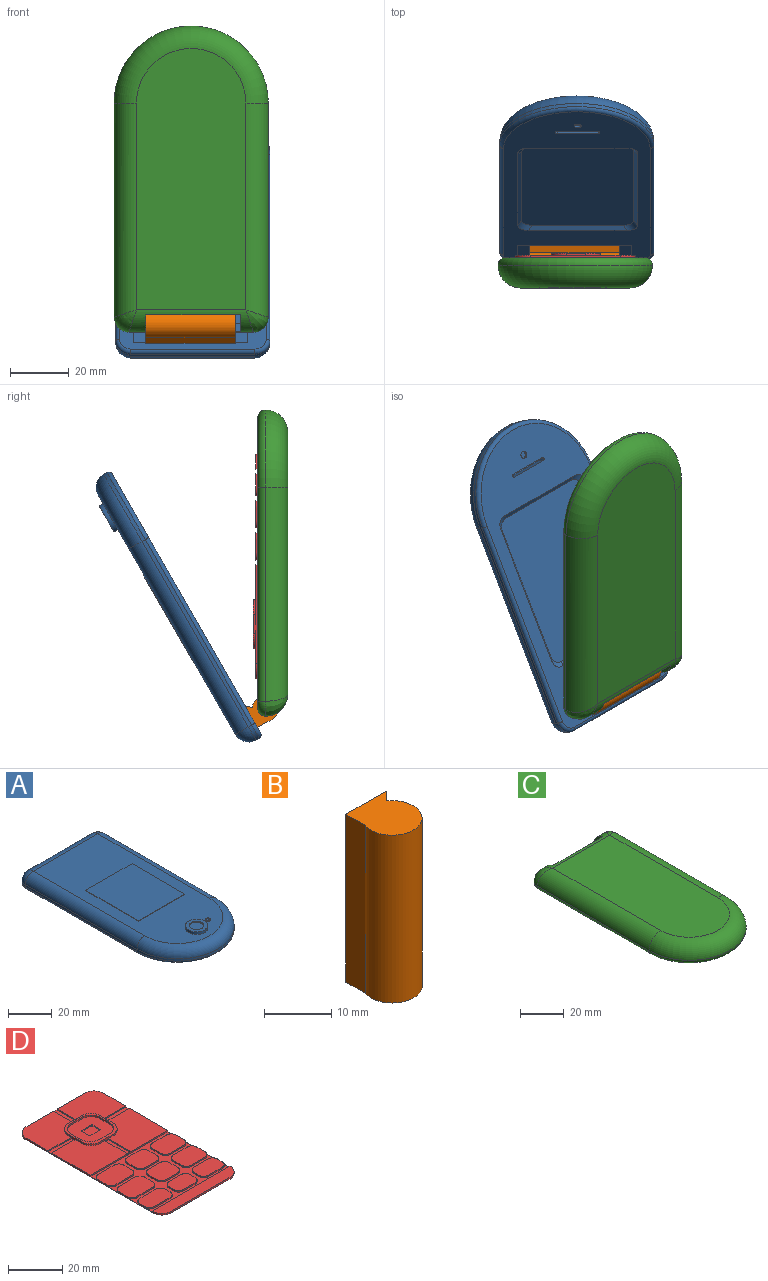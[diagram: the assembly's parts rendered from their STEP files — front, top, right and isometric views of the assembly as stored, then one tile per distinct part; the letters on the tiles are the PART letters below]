
ASSEMBLY  parts=4 mates=3
PART A: 58 faces, bbox 56.6x106.5x9.7 mm
  f0: plane 101.35x49.78mm, normal (0,0,-1), area 2202.3mm2, adj f14,f15,f16,f17,f18,f19,f21,f22
  f1: plane 42.16x1.27mm, normal (0,1,0), area 53.5mm2, adj f6,f7,f11,f17
  f2: plane 72.64x1.27mm, normal (-1,0,0), area 92.3mm2, adj f5,f6,f12,f14
  f3: plane 72.64x1.27mm, normal (1,0,0), area 92.3mm2, adj f5,f7,f8,f18
  f4: plane 93.73x42.16mm, normal (0,0,1), area 2641.5mm2, adj f8,f10,f11,f12,f43,f47,f51,f52
  f5: cylinder r=26.16mm len=52.32mm, axis (0,0,1), area 104.4mm2, adj f2,f3,f10,f16
  f6: cylinder r=5.08mm len=5.08mm, axis (0,0,1), area 10.1mm2, adj f1,f2,f13,f15
  f7: cylinder r=5.08mm len=5.08mm, axis (0,0,-1), area 10.1mm2, adj f1,f3,f9,f19
  f8: cylinder r=5.08mm len=72.64mm, axis (0,-1,0), area 579.7mm2, adj f3,f4,f9,f10
  f9: sphere r=5.08mm, area 40.5mm2, adj f7,f8,f11
  f10: torus R=21.08mm, axis (0,0,1), area 609.6mm2, adj f4,f5,f8,f12
  f11: cylinder r=5.08mm len=42.16mm, axis (1,0,0), area 336.5mm2, adj f1,f4,f9,f13
  f12: cylinder r=5.08mm len=72.64mm, axis (0,1,0), area 579.7mm2, adj f2,f4,f10,f13
  f13: sphere r=5.08mm, area 40.5mm2, adj f6,f11,f12
  f14: cylinder r=1.27mm len=72.64mm, axis (0,-1,0), area 144.9mm2, adj f0,f2,f15,f16
  f15: torus R=3.81mm, axis (0,0,1), area 14.5mm2, adj f0,f6,f14,f17
  f16: torus R=24.89mm, axis (0,0,1), area 161.1mm2, adj f0,f5,f14,f18
  f17: cylinder r=1.27mm len=42.16mm, axis (-1,0,0), area 84.1mm2, adj f0,f1,f15,f19
  f18: cylinder r=1.27mm len=72.64mm, axis (0,1,0), area 144.9mm2, adj f0,f3,f16,f19
  f19: torus R=3.81mm, axis (0,0,1), area 14.5mm2, adj f0,f7,f17,f18
  f20: plane 53.34x38.1mm, normal (0,0,-1), area 2022.6mm2, adj f21,f22,f23,f24,f25,f26,f27,f28
  f21: plane 33.46x1.27mm, normal (0,0.71,-0.71), area 57.8mm2, adj f0,f20,f25,f26
  f22: plane 48.7x1.27mm, normal (0.71,0,-0.71), area 85.2mm2, adj f0,f20,f25,f27
  f23: plane 48.7x1.27mm, normal (-0.71,0,-0.71), area 85.2mm2, adj f0,f20,f26,f28
  f24: plane 33.46x1.27mm, normal (0,-0.71,-0.71), area 57.8mm2, adj f0,f20,f27,f28
  f25: cylinder r=5.08mm len=5.42mm, axis (-0.58,-0.58,-0.58), area 11.7mm2, adj f0,f20,f21,f22
  f26: cylinder r=5.08mm len=5.42mm, axis (0.58,-0.58,-0.58), area 11.7mm2, adj f0,f20,f21,f23
  f27: cylinder r=5.08mm len=5.42mm, axis (0.58,-0.58,0.58), area 11.7mm2, adj f0,f20,f22,f24
  f28: cylinder r=5.08mm len=5.42mm, axis (-0.58,-0.58,0.58), area 11.7mm2, adj f0,f20,f23,f24
  f29: plane 38.61x0.03mm, normal (0,-1,0), area 1mm2, adj f0,f30,f32,f33
  f30: plane 7.46x0.03mm, normal (-1,0,0), area 0.2mm2, adj f0,f29,f31,f33
  f31: plane 38.61x0.03mm, normal (0,1,0), area 1mm2, adj f0,f30,f32,f33
  f32: plane 7.46x0.03mm, normal (1,0,0), area 0.2mm2, adj f0,f29,f31,f33
  f33: plane 38.61x7.46mm, normal (0,0,-1), area 287.8mm2, adj f29,f30,f31,f32
  f34: plane 13.92x2.54mm, normal (0,1,0), area 35.4mm2, adj f0,f38,f39,f42
  f35: plane 2.54x0.14mm, normal (1,0,0), area 0.4mm2, adj f0,f38,f39,f40
  f36: plane 13.92x2.54mm, normal (0,-1,0), area 35.4mm2, adj f0,f38,f40,f41
  f37: plane 2.54x0.14mm, normal (-1,0,0), area 0.4mm2, adj f0,f38,f41,f42
  f38: plane 14.94x1.16mm, normal (0,0,-1), area 17.1mm2, adj f34,f35,f36,f37,f39,f40,f41,f42
  f39: cylinder r=0.51mm len=2.54mm, axis (0,0,-1), area 2mm2, adj f0,f34,f35,f38
  f40: cylinder r=0.51mm len=2.54mm, axis (0,0,1), area 2mm2, adj f0,f35,f36,f38
  f41: cylinder r=0.51mm len=2.54mm, axis (0,0,-1), area 2mm2, adj f0,f36,f37,f38
  f42: cylinder r=0.51mm len=2.54mm, axis (0,0,1), area 2mm2, adj f0,f34,f37,f38
  f43: cylinder r=5.08mm len=10.16mm, axis (0,0,-1), area 48.6mm2, adj f4,f44
  f44: plane 10.16x10.16mm, normal (0,0,1), area 47.4mm2, adj f43,f45
  f45: cylinder r=3.27mm len=6.54mm, axis (0,0,1), area 10.4mm2, adj f44,f46
  f46: plane 6.54x6.54mm, normal (0,0,1), area 33.6mm2, adj f45
  f47: cylinder r=1.17mm len=2.35mm, axis (0,0,-1), area 2.1mm2, adj f4,f48
  f48: plane 2.35x2.35mm, normal (0,0,1), area 2.1mm2, adj f47,f49
  f49: cylinder r=0.84mm len=1.67mm, axis (0,0,1), area 1.3mm2, adj f48,f50
  f50: plane 1.67x1.67mm, normal (0,0,1), area 2.2mm2, adj f49
  f51: plane 30.08x0.25mm, normal (0,1,0), area 7.6mm2, adj f4,f52,f54,f55
  f52: plane 34.38x0.25mm, normal (-1,0,0), area 8.7mm2, adj f4,f51,f53,f55
  f53: plane 30.08x0.25mm, normal (0,-1,0), area 7.6mm2, adj f4,f52,f54,f55
  f54: plane 34.38x0.25mm, normal (1,0,0), area 8.7mm2, adj f4,f51,f53,f55
  f55: plane 34.38x30.08mm, normal (0,0,1), area 1034.3mm2, adj f51,f52,f53,f54
  f56: cylinder r=1.22mm len=2.44mm, axis (0,0,-1), area 5.8mm2, adj f0,f57
  f57: plane 2.44x2.44mm, normal (0,0,-1), area 4.7mm2, adj f56
PART B: 6 faces, bbox 8.9x10x30.5 mm
  f0: plane 30.48x4.06mm, normal (-1,0,0), area 123.9mm2, adj f1,f3,f4,f5
  f1: cylinder r=4.45mm len=30.48mm, axis (0,0,-1), area 603.2mm2, adj f0,f2,f4,f5
  f2: plane 30.48x1.83mm, normal (0.71,-0.7,0), area 78.1mm2, adj f1,f3,f4,f5
  f3: plane 30.48x8.48mm, normal (0,1,0), area 258.4mm2, adj f0,f2,f4,f5
  f4: plane 9.96x8.89mm, normal (0,0,1), area 74.9mm2, adj f0,f1,f2,f3
  f5: plane 9.96x8.89mm, normal (0,0,-1), area 74.9mm2, adj f0,f1,f2,f3
PART C: 18 faces, bbox 56.6x106.5x10.2 mm
  f0: cylinder r=7.62mm len=42.16mm, axis (1,0,0), area 181.7mm2, adj f1,f2,f5,f8,f14,f15,f16,f17
  f1: cylinder r=2.54mm len=42.16mm, axis (-1,0,0), area 56.2mm2, adj f0,f3,f11,f13,f14,f15,f16
  f2: plane 88.65x37.08mm, normal (0,0,1), area 3139.8mm2, adj f0,f4,f6,f7
  f3: plane 98.81x47.24mm, normal (0,0,-1), area 4317.7mm2, adj f1,f9,f10,f11,f12,f13,f14,f16
  f4: cylinder r=7.62mm len=72.64mm, axis (0,-1,0), area 858.5mm2, adj f2,f5,f6,f9
  f5: bspline ~9.26x7.62mm, area 62.9mm2, adj f0,f4,f11
  f6: torus R=18.54mm, axis (0,0,1), area 879.7mm2, adj f2,f4,f7,f10
  f7: cylinder r=7.62mm len=72.64mm, axis (0,1,0), area 858.5mm2, adj f2,f6,f8,f12
  f8: bspline ~9.26x7.62mm, area 62.9mm2, adj f0,f7,f13
  f9: cylinder r=2.54mm len=72.64mm, axis (0,1,0), area 289.8mm2, adj f3,f4,f10,f11
  f10: torus R=23.62mm, axis (0,0,1), area 316.4mm2, adj f3,f6,f9,f12
  f11: torus R=2.54mm, axis (0,0,1), area 26.1mm2, adj f1,f3,f5,f9
  f12: cylinder r=2.54mm len=72.64mm, axis (0,-1,0), area 289.8mm2, adj f3,f7,f10,f13
  f13: torus R=2.54mm, axis (0,0,1), area 26.1mm2, adj f1,f3,f8,f12
  f14: plane 9.96x5.84mm, normal (1,0,0), area 46.1mm2, adj f0,f1,f3,f15,f17
  f15: plane 32.22x1.4mm, normal (0,-1,0), area 45mm2, adj f0,f1,f14,f16
  f16: plane 9.96x5.84mm, normal (-1,0,0), area 46.1mm2, adj f0,f1,f3,f15,f17
  f17: plane 32.22x9.96mm, normal (0,1,0), area 320.9mm2, adj f0,f3,f14,f16
PART D: 133 faces, bbox 40.6x76.2x1.5 mm
  f0: plane 19.31x16.52mm, normal (0,0,1), area 271.5mm2, adj f1,f6,f19,f93,f96,f108,f119,f125
  f1: plane 30.48x0.76mm, normal (0,1,0), area 22.3mm2, adj f0,f2,f16,f19,f20,f124,f125,f126
  f2: plane 19.42x16.52mm, normal (0,0,1), area 275mm2, adj f1,f3,f20,f93,f94,f105,f122,f124
  f3: plane 66.04x0.76mm, normal (-1,0,0), area 36mm2, adj f2,f7,f8,f9,f10,f16,f17,f20
  f4: plane 15.24x14.73mm, normal (0,0,1), area 176.5mm2, adj f97,f98,f99,f100,f101,f102,f103,f104
  f5: plane 16.68x16.68mm, normal (0,0,1), area 53.9mm2, adj f93,f94,f95,f96,f97,f98,f99,f100
  f6: plane 66.04x0.76mm, normal (1,0,0), area 36mm2, adj f0,f7,f11,f12,f13,f16,f18,f19
  f7: plane 40.64x20.14mm, normal (0,0,1), area 668.1mm2, adj f3,f6,f30,f94,f95,f96,f106,f107
  f8: plane 13.36x9.22mm, normal (0,0,1), area 117.6mm2, adj f3,f31,f32,f33,f57,f58,f71,f74
  f9: plane 13.36x9.22mm, normal (0,0,1), area 117.6mm2, adj f3,f34,f35,f36,f72,f73,f75,f78
  f10: plane 13.36x7.46mm, normal (0,0,1), area 94mm2, adj f3,f37,f38,f39,f76,f77,f87,f88
  f11: plane 12.21x7.46mm, normal (0,0,1), area 85.5mm2, adj f6,f41,f42,f43,f84,f85,f91,f92
  f12: plane 12.21x9.22mm, normal (0,0,1), area 107mm2, adj f6,f44,f45,f46,f64,f65,f83,f86
  f13: plane 12.21x9.22mm, normal (0,0,1), area 107mm2, adj f6,f47,f48,f49,f61,f62,f63,f66
  f14: plane 40.64x5.08mm, normal (0,0,1), area 195.4mm2, adj f15,f17,f18,f40
  f15: plane 30.48x0.76mm, normal (0,-1,0), area 23.2mm2, adj f14,f16,f17,f18
  f16: plane 76.2x40.64mm, normal (0,0,-1), area 3074.6mm2, adj f1,f3,f6,f15,f17,f18,f19,f20
  f17: cylinder r=5.08mm len=5.08mm, axis (0,0,1), area 6.1mm2, adj f3,f14,f15,f16,f40
  f18: cylinder r=5.08mm len=5.08mm, axis (0,0,-1), area 6.1mm2, adj f6,f14,f15,f16,f40
  f19: cylinder r=5.08mm len=5.08mm, axis (0,0,1), area 6.1mm2, adj f0,f1,f6,f16
  f20: cylinder r=5.08mm len=5.08mm, axis (0,0,-1), area 6.1mm2, adj f1,f2,f3,f16
  f21: plane 2.38x0.61mm, normal (-1,0,0), area 1.4mm2, adj f53,f56,f80,f89
  f22: plane 5.98x0.61mm, normal (0,1,0), area 3.6mm2, adj f53,f56,f80,f81
  f23: plane 2.38x0.61mm, normal (1,0,0), area 1.4mm2, adj f53,f56,f81,f90
  f24: plane 4.14x0.61mm, normal (-1,0,0), area 2.5mm2, adj f53,f55,f68,f79
  f25: plane 5.98x0.61mm, normal (0,1,0), area 3.6mm2, adj f53,f55,f68,f69
  f26: plane 4.14x0.61mm, normal (1,0,0), area 2.5mm2, adj f53,f55,f69,f82
  f27: plane 4.14x0.61mm, normal (-1,0,0), area 2.5mm2, adj f53,f54,f59,f67
  f28: plane 5.98x0.61mm, normal (0,1,0), area 3.6mm2, adj f53,f54,f59,f60
  f29: plane 4.14x0.61mm, normal (1,0,0), area 2.5mm2, adj f53,f54,f60,f70
  f30: plane 40.64x0.61mm, normal (0,-1,0), area 24.8mm2, adj f3,f6,f7,f53
  f31: plane 8.28x0.61mm, normal (0,1,0), area 5mm2, adj f8,f53,f57,f58
  f32: plane 4.14x0.61mm, normal (1,0,0), area 2.5mm2, adj f8,f53,f58,f74
  f33: plane 8.28x0.61mm, normal (0,-1,0), area 5mm2, adj f8,f53,f71,f74
  f34: plane 8.28x0.61mm, normal (0,1,0), area 5mm2, adj f9,f53,f72,f73
  f35: plane 4.14x0.61mm, normal (1,0,0), area 2.5mm2, adj f9,f53,f73,f78
  f36: plane 8.28x0.61mm, normal (0,-1,0), area 5mm2, adj f9,f53,f75,f78
  f37: plane 8.28x0.61mm, normal (0,1,0), area 5mm2, adj f10,f53,f76,f77
  f38: plane 2.38x0.61mm, normal (1,0,0), area 1.4mm2, adj f10,f53,f77,f87
  f39: plane 8.28x0.61mm, normal (0,-1,0), area 5mm2, adj f10,f53,f87,f88
  f40: plane 40.64x0.61mm, normal (0,1,0), area 24.8mm2, adj f14,f17,f18,f53
  f41: plane 7.13x0.61mm, normal (0,-1,0), area 4.3mm2, adj f11,f53,f91,f92
  f42: plane 2.38x0.61mm, normal (-1,0,0), area 1.4mm2, adj f11,f53,f84,f91
  f43: plane 7.13x0.61mm, normal (0,1,0), area 4.3mm2, adj f11,f53,f84,f85
  f44: plane 7.13x0.61mm, normal (0,-1,0), area 4.3mm2, adj f12,f53,f83,f86
  f45: plane 4.14x0.61mm, normal (-1,0,0), area 2.5mm2, adj f12,f53,f64,f83
  f46: plane 7.13x0.61mm, normal (0,1,0), area 4.3mm2, adj f12,f53,f64,f65
  f47: plane 7.13x0.61mm, normal (0,-1,0), area 4.3mm2, adj f13,f53,f63,f66
  f48: plane 4.14x0.61mm, normal (-1,0,0), area 2.5mm2, adj f13,f53,f61,f63
  f49: plane 7.13x0.61mm, normal (0,1,0), area 4.3mm2, adj f13,f53,f61,f62
  f50: plane 5.98x0.61mm, normal (0,-1,0), area 3.6mm2, adj f53,f55,f79,f82
  f51: plane 5.98x0.61mm, normal (0,-1,0), area 3.6mm2, adj f53,f54,f67,f70
  f52: plane 5.98x0.61mm, normal (0,-1,0), area 3.6mm2, adj f53,f56,f89,f90
  f53: plane 40.64x32.43mm, normal (0,0,1), area 420mm2, adj f3,f6,f21,f22,f23,f24,f25,f26
  f54: plane 11.06x9.22mm, normal (0,0,1), area 96.4mm2, adj f27,f28,f29,f51,f59,f60,f67,f70
  f55: plane 11.06x9.22mm, normal (0,0,1), area 96.4mm2, adj f24,f25,f26,f50,f68,f69,f79,f82
  f56: plane 11.06x7.46mm, normal (0,0,1), area 76.9mm2, adj f21,f22,f23,f52,f80,f81,f89,f90
  f57: cylinder r=2.54mm len=2.54mm, axis (0,0,-1), area 2.4mm2, adj f3,f8,f31,f53
  f58: cylinder r=2.54mm len=2.54mm, axis (0,0,1), area 2.4mm2, adj f8,f31,f32,f53
  f59: cylinder r=2.54mm len=2.54mm, axis (0,0,1), area 2.4mm2, adj f27,f28,f53,f54
  f60: cylinder r=2.54mm len=2.54mm, axis (0,0,1), area 2.4mm2, adj f28,f29,f53,f54
  f61: cylinder r=2.54mm len=2.54mm, axis (0,0,1), area 2.4mm2, adj f13,f48,f49,f53
  f62: cylinder r=2.54mm len=2.54mm, axis (0,0,1), area 2.4mm2, adj f6,f13,f49,f53
  f63: cylinder r=2.54mm len=2.54mm, axis (0,0,-1), area 2.4mm2, adj f13,f47,f48,f53
  f64: cylinder r=2.54mm len=2.54mm, axis (0,0,1), area 2.4mm2, adj f12,f45,f46,f53
  f65: cylinder r=2.54mm len=2.54mm, axis (0,0,1), area 2.4mm2, adj f6,f12,f46,f53
  f66: cylinder r=2.54mm len=2.54mm, axis (0,0,-1), area 2.4mm2, adj f6,f13,f47,f53
  f67: cylinder r=2.54mm len=2.54mm, axis (0,0,-1), area 2.4mm2, adj f27,f51,f53,f54
  f68: cylinder r=2.54mm len=2.54mm, axis (0,0,1), area 2.4mm2, adj f24,f25,f53,f55
  f69: cylinder r=2.54mm len=2.54mm, axis (0,0,1), area 2.4mm2, adj f25,f26,f53,f55
  f70: cylinder r=2.54mm len=2.54mm, axis (0,0,-1), area 2.4mm2, adj f29,f51,f53,f54
  f71: cylinder r=2.54mm len=2.54mm, axis (0,0,1), area 2.4mm2, adj f3,f8,f33,f53
  f72: cylinder r=2.54mm len=2.54mm, axis (0,0,-1), area 2.4mm2, adj f3,f9,f34,f53
  f73: cylinder r=2.54mm len=2.54mm, axis (0,0,1), area 2.4mm2, adj f9,f34,f35,f53
  f74: cylinder r=2.54mm len=2.54mm, axis (0,0,-1), area 2.4mm2, adj f8,f32,f33,f53
  f75: cylinder r=2.54mm len=2.54mm, axis (0,0,1), area 2.4mm2, adj f3,f9,f36,f53
  f76: cylinder r=2.54mm len=2.54mm, axis (0,0,-1), area 2.4mm2, adj f3,f10,f37,f53
  f77: cylinder r=2.54mm len=2.54mm, axis (0,0,1), area 2.4mm2, adj f10,f37,f38,f53
  f78: cylinder r=2.54mm len=2.54mm, axis (0,0,-1), area 2.4mm2, adj f9,f35,f36,f53
  f79: cylinder r=2.54mm len=2.54mm, axis (0,0,-1), area 2.4mm2, adj f24,f50,f53,f55
  f80: cylinder r=2.54mm len=2.54mm, axis (0,0,1), area 2.4mm2, adj f21,f22,f53,f56
  f81: cylinder r=2.54mm len=2.54mm, axis (0,0,1), area 2.4mm2, adj f22,f23,f53,f56
  f82: cylinder r=2.54mm len=2.54mm, axis (0,0,-1), area 2.4mm2, adj f26,f50,f53,f55
  f83: cylinder r=2.54mm len=2.54mm, axis (0,0,-1), area 2.4mm2, adj f12,f44,f45,f53
  f84: cylinder r=2.54mm len=2.54mm, axis (0,0,1), area 2.4mm2, adj f11,f42,f43,f53
  f85: cylinder r=2.54mm len=2.54mm, axis (0,0,1), area 2.4mm2, adj f6,f11,f43,f53
  f86: cylinder r=2.54mm len=2.54mm, axis (0,0,-1), area 2.4mm2, adj f6,f12,f44,f53
  f87: cylinder r=2.54mm len=2.54mm, axis (0,0,-1), area 2.4mm2, adj f10,f38,f39,f53
  f88: cylinder r=2.54mm len=2.54mm, axis (0,0,1), area 2.4mm2, adj f3,f10,f39,f53
  f89: cylinder r=2.54mm len=2.54mm, axis (0,0,-1), area 2.4mm2, adj f21,f52,f53,f56
  f90: cylinder r=2.54mm len=2.54mm, axis (0,0,-1), area 2.4mm2, adj f23,f52,f53,f56
  f91: cylinder r=2.54mm len=2.54mm, axis (0,0,-1), area 2.4mm2, adj f11,f41,f42,f53
  f92: cylinder r=2.54mm len=2.54mm, axis (0,0,-1), area 2.4mm2, adj f6,f11,f41,f53
  f93: plane 6.52x1.27mm, normal (0,1,0), area 5.9mm2, adj f0,f2,f5,f105,f108,f124,f125,f126
  f94: plane 6.52x1.27mm, normal (-1,0,0), area 6mm2, adj f2,f5,f7,f105,f106,f121,f122,f123
  f95: plane 6.52x0.76mm, normal (0,-1,0), area 5mm2, adj f5,f7,f106,f107,f127
  f96: plane 6.52x1.27mm, normal (1,0,0), area 6mm2, adj f0,f5,f7,f107,f108,f118,f119,f120
  f97: plane 5.08x0.76mm, normal (0,-1,0), area 3.9mm2, adj f4,f5,f101,f104
  f98: plane 4.57x0.76mm, normal (1,0,0), area 3.5mm2, adj f4,f5,f101,f102
  f99: plane 5.08x0.76mm, normal (0,1,0), area 3.9mm2, adj f4,f5,f102,f103
  f100: plane 4.57x0.76mm, normal (-1,0,0), area 3.5mm2, adj f4,f5,f103,f104
  f101: cylinder r=5.08mm len=5.08mm, axis (0,0,1), area 6.1mm2, adj f4,f5,f97,f98
  f102: cylinder r=5.08mm len=5.08mm, axis (0,0,-1), area 6.1mm2, adj f4,f5,f98,f99
  f103: cylinder r=5.08mm len=5.08mm, axis (0,0,1), area 6.1mm2, adj f4,f5,f99,f100
  f104: cylinder r=5.08mm len=5.08mm, axis (0,0,-1), area 6.1mm2, adj f4,f5,f97,f100
  f105: cylinder r=5.08mm len=5.08mm, axis (0,0,1), area 6.1mm2, adj f2,f5,f93,f94
  f106: cylinder r=5.08mm len=5.08mm, axis (0,0,-1), area 6.1mm2, adj f5,f7,f94,f95
  f107: cylinder r=5.08mm len=5.08mm, axis (0,0,1), area 6.1mm2, adj f5,f7,f95,f96
  f108: cylinder r=5.08mm len=5.08mm, axis (0,0,-1), area 6.1mm2, adj f0,f5,f93,f96
  f109: plane 5.19x4.07mm, normal (0,0,1), area 20.9mm2, adj f110,f111,f112,f113,f114,f115,f116,f117
  f110: plane 3.5x0.25mm, normal (-0.71,0,0.71), area 1.2mm2, adj f4,f109,f114,f115
  f111: plane 4.62x0.25mm, normal (0,-0.71,0.71), area 1.6mm2, adj f4,f109,f114,f116
  f112: plane 4.62x0.25mm, normal (0,0.71,0.71), area 1.6mm2, adj f4,f109,f115,f117
  f113: plane 3.5x0.25mm, normal (0.71,0,0.71), area 1.2mm2, adj f4,f109,f116,f117
  f114: cylinder r=0.76mm len=0.88mm, axis (-0.58,-0.58,-0.58), area 0.4mm2, adj f4,f109,f110,f111
  f115: cylinder r=0.76mm len=0.88mm, axis (-0.58,0.58,-0.58), area 0.4mm2, adj f4,f109,f110,f112
  f116: cylinder r=0.76mm len=0.88mm, axis (-0.58,0.58,0.58), area 0.4mm2, adj f4,f109,f111,f113
  f117: cylinder r=0.76mm len=0.88mm, axis (-0.58,-0.58,0.58), area 0.4mm2, adj f4,f109,f112,f113
  f118: plane 11.79x0.51mm, normal (0,1,0), area 6mm2, adj f6,f7,f96,f120
  f119: plane 11.79x0.51mm, normal (0,-1,0), area 6mm2, adj f0,f6,f96,f120
  f120: plane 11.79x2.02mm, normal (0,0,1), area 23.8mm2, adj f6,f96,f118,f119
  f121: plane 12.17x0.51mm, normal (0,1,0), area 6.2mm2, adj f3,f7,f94,f123
  f122: plane 12.17x0.51mm, normal (0,-1,0), area 6.2mm2, adj f2,f3,f94,f123
  f123: plane 12.17x2.02mm, normal (0,0,1), area 24.6mm2, adj f3,f94,f121,f122
  f124: plane 10.2x0.51mm, normal (1,0,0), area 5.2mm2, adj f1,f2,f93,f126
  f125: plane 10.2x0.51mm, normal (-1,0,0), area 5.2mm2, adj f0,f1,f93,f126
  f126: plane 10.2x1.91mm, normal (0,0,1), area 19.5mm2, adj f1,f93,f124,f125
  f127: plane 1.91x0.05mm, normal (0,0,-1), area 0.1mm2, adj f95,f128,f129,f131
  f128: plane 1.91x0.51mm, normal (0,-1,0), area 1mm2, adj f127,f129,f131,f132
  f129: plane 11.74x0.51mm, normal (1,0,0), area 6mm2, adj f7,f127,f128,f130,f132
  f130: plane 1.91x0.51mm, normal (0,1,0), area 1mm2, adj f7,f129,f131,f132
  f131: plane 11.74x0.51mm, normal (-1,0,0), area 6mm2, adj f7,f127,f128,f130,f132
  f132: plane 11.74x1.91mm, normal (0,0,1), area 22.4mm2, adj f128,f129,f130,f131
PLACE A rot(axis=(-1,0,0),119.8deg) t=(36.76,83.39,-99.68)mm
PLACE B rot(axis=(-0.25,-0.94,0.25),93.8deg) t=(44.88,68.27,-196.33)mm
PLACE C rot(axis=(0,0.71,-0.71),180deg) t=(17.26,59.75,-82.84)mm fixed
PLACE D rot(axis=(-1,0,0),90deg) t=(-19.96,59.75,-69.24)mm
MATE fastened C.f3 <-> D.f16  axis (0,1,0) through (29.84,59.75,-86.02)mm
MATE fastened A.f33 <-> B.f3  axis (0,-0.87,0.5) through (29.64,62.01,-136.92)mm
MATE revolute C.f1 <-> B.f1  axis (1,0,0) through (14.4,57.21,-134.2)mm
